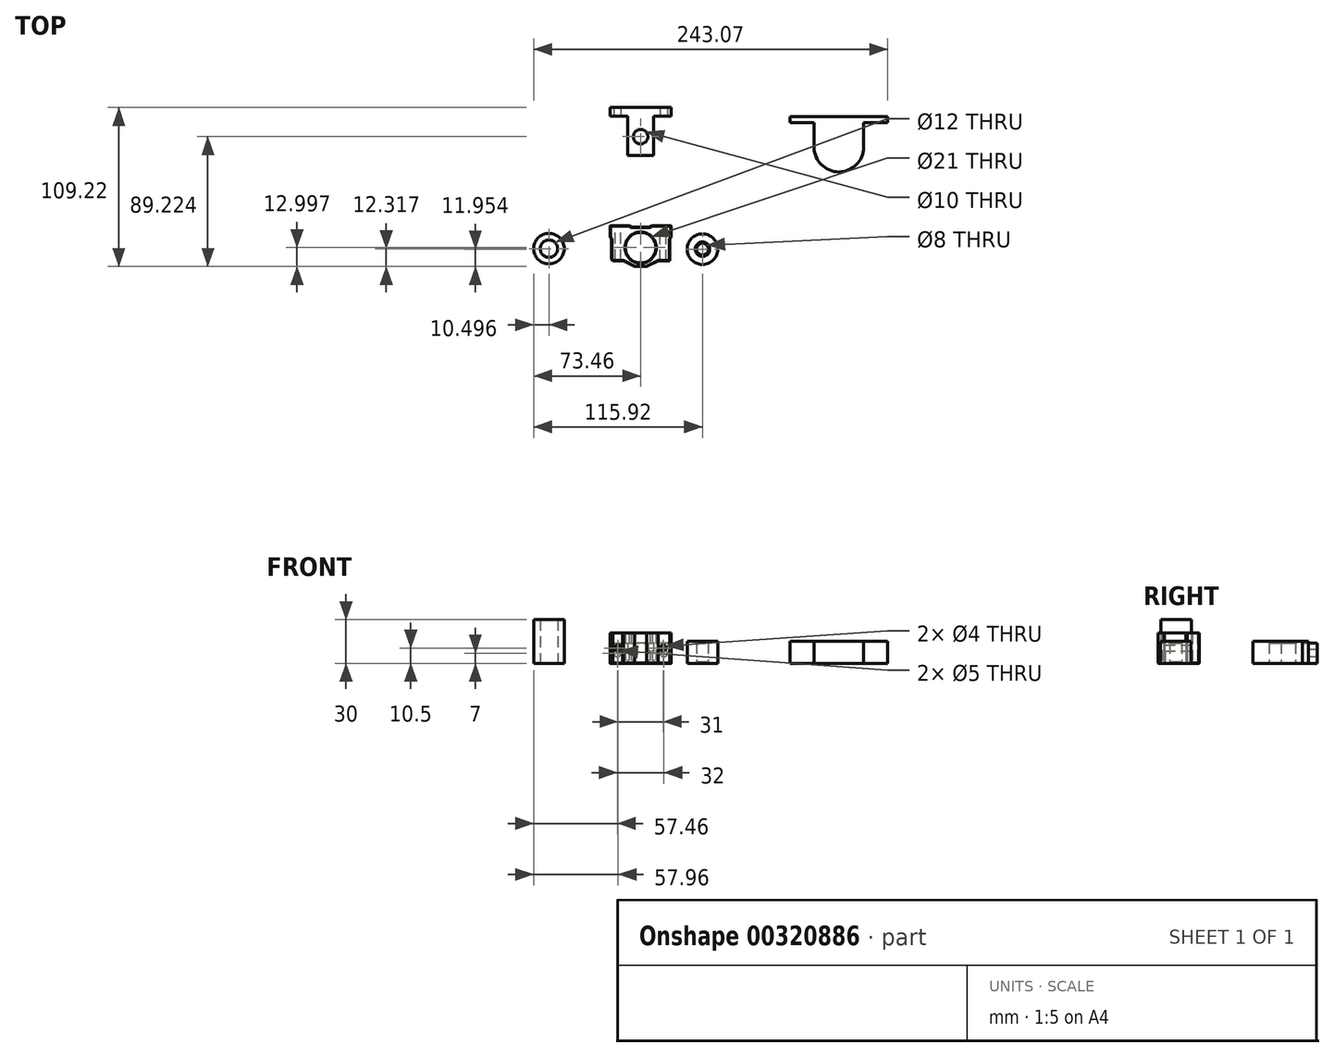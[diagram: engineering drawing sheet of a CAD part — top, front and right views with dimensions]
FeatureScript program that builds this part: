
annotation { "Feature Type Name" : "Feature", "Feature Type Description" : "" }
export const myFeature = defineFeature(function(context is Context, id is Id, definition is map)
    precondition{}
    {
        {
            var Q0;
            Q0=qCreatedBy(makeId("Top.planeOp"),FACE);
            var sketch = newSketch(context, id + "F0", { "sketchPlane" : qUnion([Q0])});
            skLineSegment(sketch, "E0", {"start": v(-21, 50.27) * mm, "end": v(21, 50.27) * mm});
            skLineSegment(sketch, "E1", {"start": v(-21, 50.27) * mm, "end": v(-21, 44.27) * mm});
            skLineSegment(sketch, "E2", {"start": v(21, 50.27) * mm, "end": v(21, 44.27) * mm});
            skLineSegment(sketch, "E3", {"start": v(-9, 17.27) * mm, "end": v(9, 17.27) * mm});
            skLineSegment(sketch, "E4", {"start": v(-9, 17.27) * mm, "end": v(-9, 44.27) * mm});
            skLineSegment(sketch, "E5", {"start": v(9, 17.27) * mm, "end": v(9, 44.27) * mm});
            skLineSegment(sketch, "E6", {"start": v(-21, 44.27) * mm, "end": v(-9, 44.27) * mm});
            skLineSegment(sketch, "E7", {"start": v(21, 44.27) * mm, "end": v(9, 44.27) * mm});
            skLineSegment(sketch, "E8", {"start": v(-21, 50.27) * mm, "end": v(0, 50.27) * mm});
            skLineSegment(sketch, "E9", {"start": v(0, 50.27) * mm, "end": v(21, 50.27) * mm});
            skCircle(sketch, "E10", {"center": v(0, 30.27) * mm, "radius": 5 * mm});
            skSolve(sketch);
        }
        {
            var Q0;
            Q0=makeQuery(id+"F0.imprint","IMPRINT",FACE,{"disambiguationData":[TD([[makeQuery(id+"F0.imprint","IMPRINT",EDGE,{"derivedFrom":sQuery(id+"F0.wireOp",EDGE,"E1")}),1.0]])]});
            extrude(context, id + "F1", {"entities" : qUnion([Q0]), "depth" : 14 * mm});
        }
        {
            var Q0;
            Q0=makeQuery(id+"F1.opExtrude","SWEPT_FACE",FACE,{"disambiguationData":[OSD([sQuery(id+"F0.wireOp",EDGE,"E6")])]});
            var sketch = newSketch(context, id + "F2", { "sketchPlane" : qUnion([Q0])});
            skCircle(sketch, "E11", {"center": v(-16, 7) * mm, "radius": 2.5 * mm});
            skCircle(sketch, "E12.MirrorC", {"center": v(16, 7) * mm, "radius": 2.5 * mm});
            skLineSegment(sketch, "E13", {"start": v(-16, 7) * mm, "end": v(-16, 0) * mm, "construction": true});
            skPoint(sketch, "E13.endSnap0", {"position": v(-15, 0) * mm});
            skLineSegment(sketch, "E14", {"start": v(-16, 7) * mm, "end": v(-16, 14) * mm, "construction": true});
            skSolve(sketch);
        }
        {
            var Q0;
            Q0 = qSketchRegion(id + "F2", true);
            extrude(context, id + "F3", {"entities" : qUnion([Q0]), "operationType" : NewBodyOperationType.REMOVE, "endBound" : BoundingType.THROUGH_ALL, "oppositeDirection" : true, "depth" : 25 * mm});
        }
        {
            var Q0;
            Q0=qCreatedBy(makeId("Top.planeOp"),FACE);
            var sketch = newSketch(context, id + "F4", { "sketchPlane" : qUnion([Q0])});
            skLineSegment(sketch, "E15", {"start": v(-21, -30.95) * mm, "end": v(-8, -30.95) * mm});
            skLineSegment(sketch, "E16", {"start": v(8, -30.95) * mm, "end": v(21, -30.95) * mm});
            skLineSegment(sketch, "E17", {"start": v(-8, -30.95) * mm, "end": v(-21, -30.95) * mm});
            skLineSegment(sketch, "E18", {"start": v(21, -30.95) * mm, "end": v(8, -30.95) * mm});
            skLineSegment(sketch, "E19", {"start": v(-6.5, -31.95) * mm, "end": v(6.5, -31.95) * mm});
            skPoint(sketch, "E20.orphan", {"position": v(0, -30.95) * mm});
            skLineSegment(sketch, "E21", {"start": v(-8, -30.95) * mm, "end": v(-6.5, -31.95) * mm});
            skLineSegment(sketch, "E22", {"start": v(6.5, -31.95) * mm, "end": v(8, -30.95) * mm});
            skLineSegment(sketch, "E23", {"start": v(-21, -30.95) * mm, "end": v(-21, -38.95) * mm});
            skLineSegment(sketch, "E24", {"start": v(21, -30.95) * mm, "end": v(21, -38.95) * mm});
            skLineSegment(sketch, "E25", {"start": v(-20, -54.95) * mm, "end": v(-12, -54.95) * mm});
            skLineSegment(sketch, "E26", {"start": v(-20, -39.95) * mm, "end": v(-20, -54.95) * mm});
            skLineSegment(sketch, "E27", {"start": v(-20, -54.95) * mm, "end": v(-20, -39.95) * mm});
            skLineSegment(sketch, "E28", {"start": v(-20, -39.95) * mm, "end": v(-21, -38.95) * mm});
            skLineSegment(sketch, "E29", {"start": v(20, -39.95) * mm, "end": v(20, -54.95) * mm});
            skLineSegment(sketch, "E30", {"start": v(20, -54.95) * mm, "end": v(20, -39.95) * mm});
            skLineSegment(sketch, "E31", {"start": v(20, -39.95) * mm, "end": v(21, -38.95) * mm});
            skLineSegment(sketch, "E32", {"start": v(20, -54.95) * mm, "end": v(12, -54.95) * mm});
            skLineSegment(sketch, "E33", {"start": v(-4, -58.95) * mm, "end": v(4, -58.95) * mm});
            skLineSegment(sketch, "E34", {"start": v(0, -58.95) * mm, "end": v(4, -58.95) * mm});
            skLineSegment(sketch, "E35", {"start": v(0, -58.95) * mm, "end": v(-4, -58.95) * mm});
            skLineSegment(sketch, "E36", {"start": v(-12, -54.95) * mm, "end": v(-4, -58.95) * mm});
            skLineSegment(sketch, "E37", {"start": v(4, -58.95) * mm, "end": v(12, -54.95) * mm});
            skLineSegment(sketch, "E38.trimOffspring", {"start": v(12, -54.95) * mm, "end": v(20, -54.95) * mm});
            skCircle(sketch, "E39", {"center": v(0, -45.95) * mm, "radius": 10.5 * mm});
            skSolve(sketch);
        }
        {
            var Q0;
            Q0 = qSketchRegion(id + "F4", true);
            extrude(context, id + "F5", {"entities" : qUnion([Q0]), "depth" : 21 * mm});
        }
        {
            var Q0;
            Q0=makeQuery(id+"F5.opExtrude","SWEPT_EDGE",EDGE,{"disambiguationData":[OSD([sQuery(id+"F4.wireOp",EDGE,"E27"),sQuery(id+"F4.wireOp",EDGE,"E25")])]});
            var Q1;
            Q1=makeQuery(id+"F5.opExtrude","SWEPT_EDGE",EDGE,{"disambiguationData":[OSD([sQuery(id+"F4.wireOp",EDGE,"E30"),sQuery(id+"F4.wireOp",EDGE,"E38.trimOffspring")])]});
            chamfer(context, id + "F6", {"entities" : qUnion([Q0, Q1]), "width" : 1 * mm, "tangentPropagation" : true});
        }
        {
            var Q0;
            Q0=makeQuery(id+"F5.opExtrude","SWEPT_FACE",FACE,{"disambiguationData":[OSD([sQuery(id+"F4.wireOp",EDGE,"E15")])]});
            var sketch = newSketch(context, id + "F7", { "sketchPlane" : qUnion([Q0])});
            skCircle(sketch, "E40", {"center": v(15.5, 10.5) * mm, "radius": 2 * mm});
            skCircle(sketch, "E41.MirrorC", {"center": v(-15.5, 10.5) * mm, "radius": 2 * mm});
            skSolve(sketch);
        }
        {
            var Q0;
            Q0 = qSketchRegion(id + "F7", true);
            extrude(context, id + "F8", {"entities" : qUnion([Q0]), "operationType" : NewBodyOperationType.REMOVE, "endBound" : BoundingType.THROUGH_ALL, "oppositeDirection" : true, "depth" : 25 * mm});
        }
        {
            var Q0;
            Q0=makeQuery(id+"F5.opExtrude","CAP_FACE",FACE,{"disambiguationData":[OSD([sQuery(id+"F4.wireOp",EDGE,"E15"),sQuery(id+"F4.wireOp",EDGE,"E19"),sQuery(id+"F4.wireOp",EDGE,"E16"),sQuery(id+"F4.wireOp",EDGE,"E21"),sQuery(id+"F4.wireOp",EDGE,"E22"),sQuery(id+"F4.wireOp",EDGE,"E23"),sQuery(id+"F4.wireOp",EDGE,"E24"),sQuery(id+"F4.wireOp",EDGE,"E27"),sQuery(id+"F4.wireOp",EDGE,"E28"),sQuery(id+"F4.wireOp",EDGE,"E30"),sQuery(id+"F4.wireOp",EDGE,"E31"),sQuery(id+"F4.wireOp",EDGE,"E25"),sQuery(id+"F4.wireOp",EDGE,"E34"),sQuery(id+"F4.wireOp",EDGE,"E35"),sQuery(id+"F4.wireOp",EDGE,"E36"),sQuery(id+"F4.wireOp",EDGE,"E37"),sQuery(id+"F4.wireOp",EDGE,"E38.trimOffspring"),sQuery(id+"F4.wireOp",EDGE,"E39")])],"isStart":false});
            var Q1;
            Q1=makeQuery(id+"F5.opExtrude","CAP_FACE",FACE,{"disambiguationData":[OSD([sQuery(id+"F4.wireOp",EDGE,"E15"),sQuery(id+"F4.wireOp",EDGE,"E19"),sQuery(id+"F4.wireOp",EDGE,"E16"),sQuery(id+"F4.wireOp",EDGE,"E21"),sQuery(id+"F4.wireOp",EDGE,"E22"),sQuery(id+"F4.wireOp",EDGE,"E23"),sQuery(id+"F4.wireOp",EDGE,"E24"),sQuery(id+"F4.wireOp",EDGE,"E27"),sQuery(id+"F4.wireOp",EDGE,"E28"),sQuery(id+"F4.wireOp",EDGE,"E30"),sQuery(id+"F4.wireOp",EDGE,"E31"),sQuery(id+"F4.wireOp",EDGE,"E25"),sQuery(id+"F4.wireOp",EDGE,"E34"),sQuery(id+"F4.wireOp",EDGE,"E35"),sQuery(id+"F4.wireOp",EDGE,"E36"),sQuery(id+"F4.wireOp",EDGE,"E37"),sQuery(id+"F4.wireOp",EDGE,"E38.trimOffspring"),sQuery(id+"F4.wireOp",EDGE,"E39")])],"isStart":true});
            var Q2;
            Q2=makeQuery(id+"F5.opExtrude","SWEPT_EDGE",EDGE,{"disambiguationData":[OSD([sQuery(id+"F4.wireOp",EDGE,"E16"),sQuery(id+"F4.wireOp",EDGE,"E24")])]});
            var Q3;
            Q3=makeQuery(id+"F5.opExtrude","SWEPT_EDGE",EDGE,{"disambiguationData":[OSD([sQuery(id+"F4.wireOp",EDGE,"E15"),sQuery(id+"F4.wireOp",EDGE,"E23")])]});
            var Q4;
            Q4=makeQuery(id+"F8.boolean.opBoolean","INTERSECT",EDGE,{"derivedFrom":[makeQuery(id+"F5.opExtrude","SWEPT_FACE",FACE,{"disambiguationData":[OSD([sQuery(id+"F4.wireOp",EDGE,"E25")])]}),makeQuery(id+"F8.opExtrude","SWEPT_FACE",FACE,{"disambiguationData":[OSD([sQuery(id+"F7.wireOp",EDGE,"E40")])]})]});
            var Q5;
            Q5=makeQuery(id+"F8.boolean.opBoolean","INTERSECT",EDGE,{"derivedFrom":[makeQuery(id+"F5.opExtrude","SWEPT_FACE",FACE,{"disambiguationData":[OSD([sQuery(id+"F4.wireOp",EDGE,"E38.trimOffspring")])]}),makeQuery(id+"F8.opExtrude","SWEPT_FACE",FACE,{"disambiguationData":[OSD([sQuery(id+"F7.wireOp",EDGE,"E41.MirrorC")])]})]});
            var Q6;
            Q6=makeQuery(id+"F8.boolean.opBoolean","COPY",EDGE,{"derivedFrom":makeQuery(id+"F8.opExtrude","CAP_EDGE",EDGE,{"disambiguationData":[OSD([sQuery(id+"F7.wireOp",EDGE,"E41.MirrorC")])],"isStart":true})});
            var Q7;
            Q7=makeQuery(id+"F8.boolean.opBoolean","COPY",EDGE,{"derivedFrom":makeQuery(id+"F8.opExtrude","CAP_EDGE",EDGE,{"disambiguationData":[OSD([sQuery(id+"F7.wireOp",EDGE,"E40")])],"isStart":true})});
            chamfer(context, id + "F9", {"entities" : qUnion([Q0, Q1, Q2, Q3, Q4, Q5, Q6, Q7]), "width" : 0.25 * mm, "tangentPropagation" : true});
        }
        {
            var Q0;
            Q0=qCreatedBy(makeId("Top.planeOp"),FACE);
            var sketch = newSketch(context, id + "F10", { "sketchPlane" : qUnion([Q0])});
            skCircle(sketch, "E42", {"center": v(42.46, -47) * mm, "radius": 10.5 * mm});
            skCircle(sketch, "E43", {"center": v(42.46, -47) * mm, "radius": 4 * mm});
            skSolve(sketch);
        }
        {
            var Q0;
            Q0 = qSketchRegion(id + "F10", true);
            extrude(context, id + "F11", {"entities" : qUnion([Q0]), "depth" : 15 * mm});
        }
        {
            var Q0;
            Q0=makeQuery(id+"F11.opExtrude","CAP_EDGE",EDGE,{"disambiguationData":[OSD([sQuery(id+"F10.wireOp",EDGE,"E43")])],"isStart":false});
            var Q1;
            Q1=makeQuery(id+"F11.opExtrude","CAP_EDGE",EDGE,{"disambiguationData":[OSD([sQuery(id+"F10.wireOp",EDGE,"E43")])],"isStart":true});
            chamfer(context, id + "F12", {"entities" : qUnion([Q0, Q1]), "width" : 1 * mm, "tangentPropagation" : true});
        }
        {
            var Q0;
            Q0=qCreatedBy(makeId("Top.planeOp"),FACE);
            var sketch = newSketch(context, id + "F13", { "sketchPlane" : qUnion([Q0])});
            skCircle(sketch, "E44", {"center": v(-62.96, -46.63) * mm, "radius": 10.5 * mm});
            skCircle(sketch, "E45", {"center": v(-62.96, -46.63) * mm, "radius": 6 * mm});
            skSolve(sketch);
        }
        {
            var Q0;
            Q0 = qSketchRegion(id + "F13", true);
            extrude(context, id + "F14", {"entities" : qUnion([Q0]), "depth" : 30 * mm});
        }
        {
            var Q0;
            Q0=qCreatedBy(makeId("Top.planeOp"),FACE);
            var sketch = newSketch(context, id + "F15", { "sketchPlane" : qUnion([Q0])});
            skCircle(sketch, "E46", {"center": v(136.1, 23.08) * mm, "radius": 17 * mm});
            skLineSegment(sketch, "E47", {"start": v(136.1, 40.08) * mm, "end": v(169.6, 40.08) * mm});
            skLineSegment(sketch, "E48", {"start": v(136.1, 40.08) * mm, "end": v(102.6, 40.08) * mm});
            skLineSegment(sketch, "E49", {"start": v(102.6, 40.08) * mm, "end": v(102.6, 44.08) * mm});
            skLineSegment(sketch, "E50", {"start": v(102.6, 44.08) * mm, "end": v(169.6, 44.08) * mm});
            skLineSegment(sketch, "E51", {"start": v(169.6, 40.08) * mm, "end": v(169.6, 44.08) * mm});
            skLineSegment(sketch, "E52", {"start": v(153.1, 23.08) * mm, "end": v(153.1, 40.08) * mm});
            skLineSegment(sketch, "E53", {"start": v(119.1, 23.08) * mm, "end": v(119.1, 40.08) * mm});
            skSolve(sketch);
        }
        {
            var Q0;
            Q0 = qSketchRegion(id + "F15", true);
            extrude(context, id + "F16", {"entities" : qUnion([Q0]), "depth" : 15 * mm});
        }
    });
